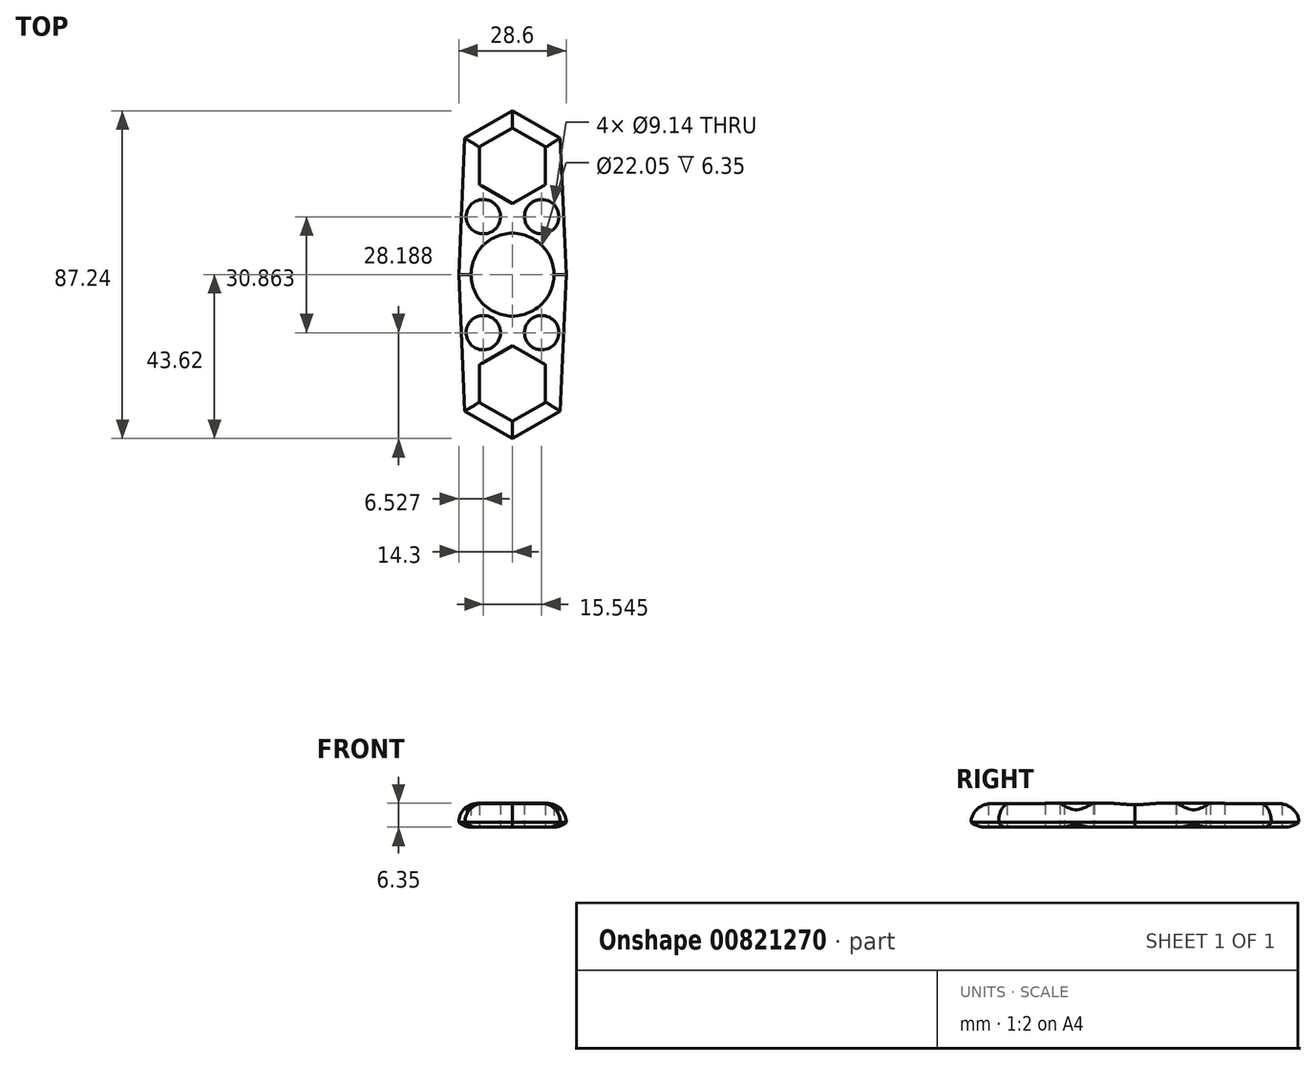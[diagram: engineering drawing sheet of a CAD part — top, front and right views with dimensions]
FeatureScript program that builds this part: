
annotation { "Feature Type Name" : "Feature", "Feature Type Description" : "" }
export const myFeature = defineFeature(function(context is Context, id is Id, definition is map)
    precondition{}
    {
        {
            var Q0;
            Q0=qCreatedBy(makeId("Top.planeOp"),FACE);
            var sketch = newSketch(context, id + "F0", { "sketchPlane" : qUnion([Q0])});
            skCircle(sketch, "E0", {"center": v(0, 0) * mm, "radius": 14.29 * mm});
            skCircle(sketch, "E1", {"center": v(0, 0) * mm, "radius": 11.02 * mm});
            skCircle(sketch, "E2.cCircle", {"center": v(0, 28.95) * mm, "radius": 12.7 * mm, "construction": true});
            skLineSegment(sketch, "E2.0", {"start": v(0, 14.29) * mm, "end": v(-12.7, 21.62) * mm});
            skLineSegment(sketch, "E2.1", {"start": v(-12.7, 21.62) * mm, "end": v(-12.7, 36.28) * mm});
            skLineSegment(sketch, "E2.2", {"start": v(-12.7, 36.28) * mm, "end": v(0, 43.62) * mm});
            skLineSegment(sketch, "E2.3", {"start": v(0, 43.62) * mm, "end": v(12.7, 36.28) * mm});
            skLineSegment(sketch, "E2.4", {"start": v(12.7, 36.28) * mm, "end": v(12.7, 21.62) * mm});
            skLineSegment(sketch, "E2.5", {"start": v(12.7, 21.62) * mm, "end": v(0, 14.29) * mm});
            skPoint(sketch, "E2.0.midPoint", {"position": v(-6.35, 17.95) * mm});
            skCircle(sketch, "E3.cCircle", {"center": v(0, 28.95) * mm, "radius": 8.74 * mm, "construction": true});
            skLineSegment(sketch, "E3.0", {"start": v(-8.74, 23.9) * mm, "end": v(-8.74, 34) * mm});
            skLineSegment(sketch, "E3.1", {"start": v(-8.74, 34) * mm, "end": v(0, 39.04) * mm});
            skLineSegment(sketch, "E3.2", {"start": v(0, 39.04) * mm, "end": v(8.74, 34) * mm});
            skLineSegment(sketch, "E3.3", {"start": v(8.74, 34) * mm, "end": v(8.74, 23.9) * mm});
            skLineSegment(sketch, "E3.4", {"start": v(8.74, 23.9) * mm, "end": v(0, 18.86) * mm});
            skLineSegment(sketch, "E3.5", {"start": v(0, 18.86) * mm, "end": v(-8.74, 23.9) * mm});
            skPoint(sketch, "E3.0.midPoint", {"position": v(-8.74, 28.95) * mm});
            skLineSegment(sketch, "E4.1.0", {"start": v(-8.74, -23.9) * mm, "end": v(0, -18.86) * mm});
            skCircle(sketch, "E4.1.1", {"center": v(0, -28.95) * mm, "radius": 8.74 * mm, "construction": true});
            skLineSegment(sketch, "E4.1.2", {"start": v(-12.7, -21.62) * mm, "end": v(0, -14.29) * mm});
            skLineSegment(sketch, "E4.1.3", {"start": v(-8.74, -34) * mm, "end": v(-8.74, -23.9) * mm});
            skLineSegment(sketch, "E4.1.4", {"start": v(-12.7, -36.28) * mm, "end": v(-12.7, -21.62) * mm});
            skPoint(sketch, "E4.1.5", {"position": v(8.74, -28.95) * mm});
            skCircle(sketch, "E4.1.6", {"center": v(0, -28.95) * mm, "radius": 12.7 * mm, "construction": true});
            skLineSegment(sketch, "E4.1.7", {"start": v(0, -43.62) * mm, "end": v(-12.7, -36.28) * mm});
            skLineSegment(sketch, "E4.1.8", {"start": v(12.7, -36.28) * mm, "end": v(0, -43.62) * mm});
            skPoint(sketch, "E4.1.9", {"position": v(6.35, -17.95) * mm});
            skLineSegment(sketch, "E4.1.10", {"start": v(0, -39.04) * mm, "end": v(-8.74, -34) * mm});
            skLineSegment(sketch, "E4.1.11", {"start": v(12.7, -21.62) * mm, "end": v(12.7, -36.28) * mm});
            skLineSegment(sketch, "E4.1.12", {"start": v(0, -14.29) * mm, "end": v(12.7, -21.62) * mm});
            skLineSegment(sketch, "E4.1.13", {"start": v(8.74, -23.9) * mm, "end": v(8.74, -34) * mm});
            skLineSegment(sketch, "E4.1.14", {"start": v(8.74, -34) * mm, "end": v(0, -39.04) * mm});
            skLineSegment(sketch, "E4.1.15", {"start": v(0, -18.86) * mm, "end": v(8.74, -23.9) * mm});
            skLineSegment(sketch, "E5", {"start": v(-12.7, 36.28) * mm, "end": v(-14.3, 0) * mm});
            skLineSegment(sketch, "E6", {"start": v(-14.3, 0) * mm, "end": v(-12.7, -36.28) * mm});
            skLineSegment(sketch, "E7", {"start": v(12.7, 36.28) * mm, "end": v(14.3, 0) * mm});
            skLineSegment(sketch, "E8", {"start": v(14.3, 0) * mm, "end": v(12.7, -36.28) * mm});
            skCircle(sketch, "E9", {"center": v(-9.43, -15.39) * mm, "radius": 3.18 * mm, "construction": true});
            skCircle(sketch, "E10.MirrorC", {"center": v(-9.43, 15.39) * mm, "radius": 3.18 * mm, "construction": true});
            skCircle(sketch, "E11.MirrorC", {"center": v(9.43, -15.39) * mm, "radius": 3.18 * mm, "construction": true});
            skCircle(sketch, "E12.MirrorC", {"center": v(9.43, 15.39) * mm, "radius": 3.18 * mm, "construction": true});
            skSolve(sketch);
        }
        {
            var Q0;
            {var subQ0=sQuery(id+"F0.wireOp",EDGE,"E5");var subQ1=sQuery(id+"F0.wireOp",EDGE,"E0");var subQ2=makeQuery(id+"F0.imprint","INTERSECT",VERTEX,{"derivedFrom":[subQ1,subQ0]});Q0=makeQuery(id+"F0.imprint","IMPRINT",FACE,{"disambiguationData":[TD([[makeQuery(id+"F0.imprint","IMPRINT",EDGE,{"disambiguationData":[TD([[subQ2,-1.0]])],"derivedFrom":subQ1}),-1.0]])]});}
            var Q1;
            {var subQ0=sQuery(id+"F0.wireOp",EDGE,"E7");var subQ1=sQuery(id+"F0.wireOp",EDGE,"E0");var subQ2=makeQuery(id+"F0.imprint","INTERSECT",VERTEX,{"derivedFrom":[subQ1,subQ0]});Q1=makeQuery(id+"F0.imprint","IMPRINT",FACE,{"disambiguationData":[TD([[makeQuery(id+"F0.imprint","IMPRINT",EDGE,{"disambiguationData":[TD([[subQ2,1.0]])],"derivedFrom":subQ1}),-1.0]])]});}
            var Q2;
            {var subQ0=sQuery(id+"F0.wireOp",EDGE,"E4.1.2");Q2=makeQuery(id+"F0.imprint","IMPRINT",FACE,{"disambiguationData":[TD([[makeQuery(id+"F0.imprint","IMPRINT",EDGE,{"derivedFrom":subQ0}),1.0]])]});}
            var Q3;
            {var subQ4=sQuery(id+"F0.wireOp",EDGE,"E4.1.11");Q3=makeQuery(id+"F0.imprint","IMPRINT",FACE,{"disambiguationData":[TD([[makeQuery(id+"F0.imprint","IMPRINT",EDGE,{"derivedFrom":subQ4}),1.0]])]});}
            var Q4;
            Q4=makeQuery(id+"F0.imprint","IMPRINT",FACE,{"disambiguationData":[TD([[makeQuery(id+"F0.imprint","IMPRINT",EDGE,{"derivedFrom":sQuery(id+"F0.wireOp",EDGE,"E2.0")}),-1.0]])]});
            var Q5;
            Q5=makeQuery(id+"F0.imprint","IMPRINT",FACE,{"disambiguationData":[TD([[makeQuery(id+"F0.imprint","IMPRINT",EDGE,{"derivedFrom":sQuery(id+"F0.wireOp",EDGE,"E4.1.0")}),1.0]])]});
            var Q6;
            Q6=makeQuery(id+"F0.imprint","IMPRINT",FACE,{"disambiguationData":[TD([[makeQuery(id+"F0.imprint","IMPRINT",EDGE,{"derivedFrom":sQuery(id+"F0.wireOp",EDGE,"E1")}),-1.0]])]});
            var Q7;
            {var subQ0=sQuery(id+"F0.wireOp",EDGE,"E2.0");Q7=makeQuery(id+"F0.imprint","IMPRINT",FACE,{"disambiguationData":[TD([[makeQuery(id+"F0.imprint","IMPRINT",EDGE,{"derivedFrom":subQ0}),1.0]])]});}
            var Q8;
            {var subQ4=sQuery(id+"F0.wireOp",EDGE,"E2.4");Q8=makeQuery(id+"F0.imprint","IMPRINT",FACE,{"disambiguationData":[TD([[makeQuery(id+"F0.imprint","IMPRINT",EDGE,{"derivedFrom":subQ4}),1.0]])]});}
            extrude(context, id + "F1", {"entities" : qUnion([Q0, Q1, Q2, Q3, Q4, Q5, Q6, Q7, Q8]), "depth" : 6.35 * mm, "offsetDistance" : 25.4 * mm});
        }
        {
            var Q0;
            Q0=qCreatedBy(makeId("Top.planeOp"),FACE);
            var sketch = newSketch(context, id + "F2", { "sketchPlane" : qUnion([Q0])});
            skCircle(sketch, "E13", {"center": v(-7.77, 15.43) * mm, "radius": 4.57 * mm});
            skCircle(sketch, "E14.MirrorC", {"center": v(7.77, 15.43) * mm, "radius": 4.57 * mm});
            skCircle(sketch, "E15.MirrorC", {"center": v(-7.77, -15.43) * mm, "radius": 4.57 * mm});
            skCircle(sketch, "E16.MirrorC", {"center": v(7.77, -15.43) * mm, "radius": 4.57 * mm});
            skSolve(sketch);
        }
        {
            var Q0;
            Q0=qSketchRegion(id+"F2",true);
            extrude(context, id + "F3", {"entities" : qUnion([Q0]), "operationType" : NewBodyOperationType.REMOVE, "endBound" : BoundingType.THROUGH_ALL, "depth" : 25.4 * mm, "offsetDistance" : 25.4 * mm});
        }
        {
            var Q0;
            Q0=makeQuery(id+"F1.opExtrude","CAP_EDGE",EDGE,{"disambiguationData":[OSD([sQuery(id+"F0.wireOp",EDGE,"E2.2")])],"isStart":false});
            var Q1;
            Q1=makeQuery(id+"F1.opExtrude","CAP_EDGE",EDGE,{"disambiguationData":[OSD([sQuery(id+"F0.wireOp",EDGE,"E2.3")])],"isStart":false});
            var Q2;
            Q2=makeQuery(id+"F1.opExtrude","CAP_EDGE",EDGE,{"disambiguationData":[OSD([sQuery(id+"F0.wireOp",EDGE,"E7")])],"isStart":false});
            var Q3;
            Q3=makeQuery(id+"F1.opExtrude","CAP_EDGE",EDGE,{"disambiguationData":[OSD([sQuery(id+"F0.wireOp",EDGE,"E8")])],"isStart":false});
            var Q4;
            Q4=makeQuery(id+"F1.opExtrude","CAP_EDGE",EDGE,{"disambiguationData":[OSD([sQuery(id+"F0.wireOp",EDGE,"E4.1.8")])],"isStart":false});
            var Q5;
            Q5=makeQuery(id+"F1.opExtrude","CAP_EDGE",EDGE,{"disambiguationData":[OSD([sQuery(id+"F0.wireOp",EDGE,"E4.1.7")])],"isStart":false});
            var Q6;
            Q6=makeQuery(id+"F1.opExtrude","CAP_EDGE",EDGE,{"disambiguationData":[OSD([sQuery(id+"F0.wireOp",EDGE,"E6")])],"isStart":false});
            var Q7;
            Q7=makeQuery(id+"F1.opExtrude","CAP_EDGE",EDGE,{"disambiguationData":[OSD([sQuery(id+"F0.wireOp",EDGE,"E5")])],"isStart":false});
            fillet(context, id + "F4", {"entities" : qUnion([Q0, Q1, Q2, Q3, Q4, Q5, Q6, Q7]), "radius" : 5.08 * mm, "tangentPropagation" : true, "allowEdgeOverflow" : false});
        }
        {
            var Q0;
            Q0=makeQuery(id+"F1.opExtrude","CAP_EDGE",EDGE,{"disambiguationData":[OSD([sQuery(id+"F0.wireOp",EDGE,"E7")])],"isStart":true});
            var Q1;
            Q1=makeQuery(id+"F1.opExtrude","CAP_EDGE",EDGE,{"disambiguationData":[OSD([sQuery(id+"F0.wireOp",EDGE,"E2.3")])],"isStart":true});
            var Q2;
            Q2=makeQuery(id+"F1.opExtrude","CAP_EDGE",EDGE,{"disambiguationData":[OSD([sQuery(id+"F0.wireOp",EDGE,"E2.2")])],"isStart":true});
            var Q3;
            Q3=makeQuery(id+"F1.opExtrude","CAP_EDGE",EDGE,{"disambiguationData":[OSD([sQuery(id+"F0.wireOp",EDGE,"E5")])],"isStart":true});
            var Q4;
            Q4=makeQuery(id+"F1.opExtrude","CAP_EDGE",EDGE,{"disambiguationData":[OSD([sQuery(id+"F0.wireOp",EDGE,"E6")])],"isStart":true});
            var Q5;
            Q5=makeQuery(id+"F1.opExtrude","CAP_EDGE",EDGE,{"disambiguationData":[OSD([sQuery(id+"F0.wireOp",EDGE,"E4.1.7")])],"isStart":true});
            var Q6;
            Q6=makeQuery(id+"F1.opExtrude","CAP_EDGE",EDGE,{"disambiguationData":[OSD([sQuery(id+"F0.wireOp",EDGE,"E4.1.8")])],"isStart":true});
            var Q7;
            Q7=makeQuery(id+"F1.opExtrude","CAP_EDGE",EDGE,{"disambiguationData":[OSD([sQuery(id+"F0.wireOp",EDGE,"E8")])],"isStart":true});
            fillet(context, id + "F5", {"entities" : qUnion([Q0, Q1, Q2, Q3, Q4, Q5, Q6, Q7]), "radius" : 5.08 * mm, "tangentPropagation" : true, "allowEdgeOverflow" : false});
        }
    });
